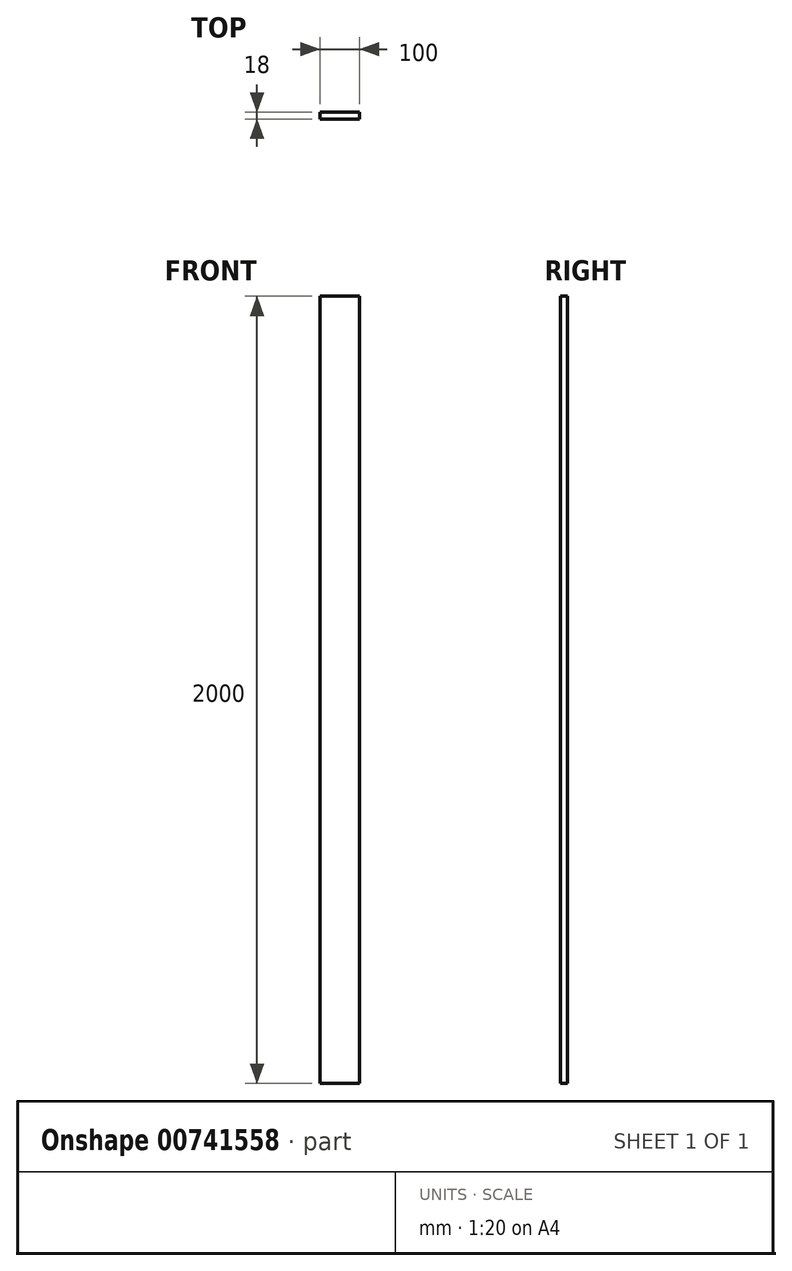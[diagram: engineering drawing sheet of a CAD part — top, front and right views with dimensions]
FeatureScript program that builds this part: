
annotation { "Feature Type Name" : "Feature", "Feature Type Description" : "" }
export const myFeature = defineFeature(function(context is Context, id is Id, definition is map)
    precondition{}
    {
        {
            var Q0;
            Q0=qCreatedBy(makeId("Front.planeOp"),FACE);
            var sketch = newSketch(context, id + "F0", { "sketchPlane" : qUnion([Q0])});
            skLineSegment(sketch, "E0.bottom", {"start": v(-50, -1000) * mm, "end": v(50, -1000) * mm});
            skLineSegment(sketch, "E0.top", {"start": v(-50, 1000) * mm, "end": v(50, 1000) * mm});
            skLineSegment(sketch, "E0.left", {"start": v(-50, -1000) * mm, "end": v(-50, 1000) * mm});
            skLineSegment(sketch, "E0.right", {"start": v(50, -1000) * mm, "end": v(50, 1000) * mm});
            skPoint(sketch, "E0.middle", {"position": v(0, 0) * mm});
            skSolve(sketch);
        }
        {
            var Q0;
            Q0=qSketchRegion(id+"F0",true);
            extrude(context, id + "F1", {"entities" : qUnion([Q0]), "oppositeDirection" : true, "depth" : 18 * mm, "offsetDistance" : 25 * mm});
        }
    });
